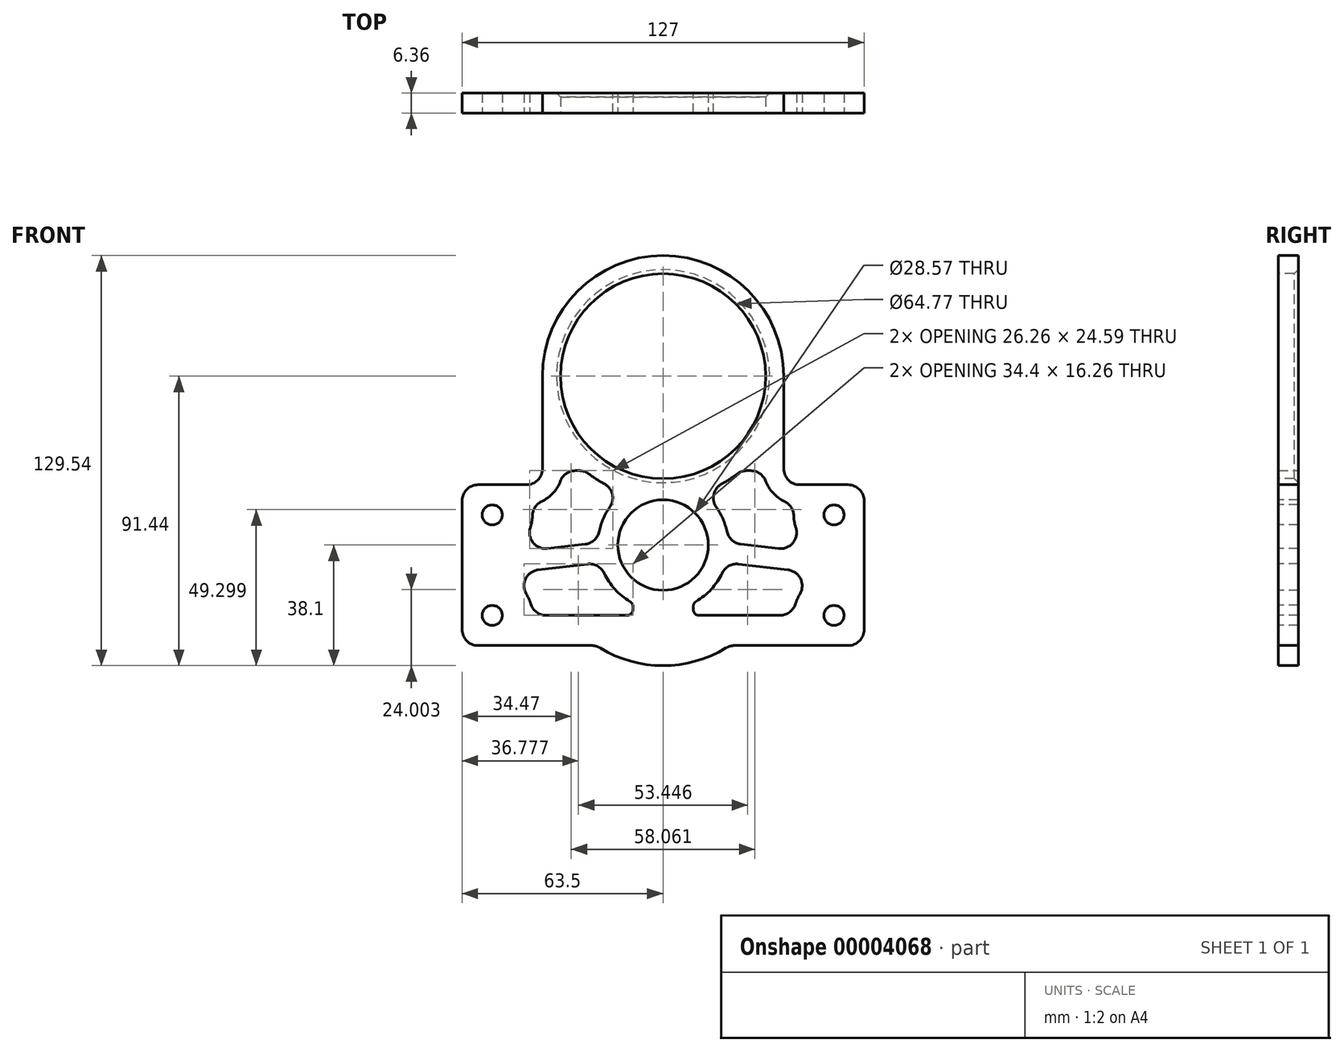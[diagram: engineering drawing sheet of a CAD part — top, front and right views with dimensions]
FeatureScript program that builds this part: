
annotation { "Feature Type Name" : "Feature", "Feature Type Description" : "" }
export const myFeature = defineFeature(function(context is Context, id is Id, definition is map)
    precondition{}
    {
        {
            var Q0;
            Q0=qCreatedBy(makeId("Front.planeOp"),FACE);
            var sketch = newSketch(context, id + "F0", { "sketchPlane" : qUnion([Q0])});
            skCircle(sketch, "E0", {"center": v(0, 0) * mm, "radius": 45.72 * mm, "construction": true});
            skCircle(sketch, "E1", {"center": v(0, 53.34) * mm, "radius": 7.62 * mm, "construction": true});
            skLineSegment(sketch, "E2", {"start": v(-38.1, 0) * mm, "end": v(-38.1, 53.34) * mm});
            skLineSegment(sketch, "E3", {"start": v(-38.1, 53.34) * mm, "end": v(0, 53.34) * mm, "construction": true});
            skLineSegment(sketch, "E4", {"start": v(0, 53.34) * mm, "end": v(38.1, 53.34) * mm, "construction": true});
            skLineSegment(sketch, "E5", {"start": v(38.1, 53.34) * mm, "end": v(38.1, 0) * mm});
            skArc(sketch, "E6", {"start": v(38.1, 53.34) * mm, "mid": v(0, 91.44) * mm, "end": v(-38.1, 53.34) * mm});
            skArc(sketch, "E7", {"start": v(-38.1, 0) * mm, "mid": v(0, -38.1) * mm, "end": v(38.1, 0) * mm});
            skCircle(sketch, "E8", {"center": v(0, 53.34) * mm, "radius": 25.4 * mm, "construction": true});
            skCircle(sketch, "E9", {"center": v(-25.4, 53.34) * mm, "radius": 2.54 * mm, "construction": true});
            skCircle(sketch, "E10", {"center": v(25.4, 53.34) * mm, "radius": 2.54 * mm, "construction": true});
            skSolve(sketch);
        }
        {
            var Q0;
            Q0=makeQuery(id+"F0.imprint","IMPRINT",FACE,{"disambiguationData":[TD([[makeQuery(id+"F0.imprint","IMPRINT",EDGE,{"derivedFrom":sQuery(id+"F0.wireOp",EDGE,"E2")}),-1.0]])]});
            extrude(context, id + "F1", {"entities" : qUnion([Q0]), "endBound" : BoundingType.SYMMETRIC, "depth" : 6.35 * mm});
        }
        {
            var Q0;
            Q0=makeQuery(id+"F1.opExtrude","CAP_FACE",FACE,{"disambiguationData":[OSD([sQuery(id+"F0.wireOp",EDGE,"E2"),sQuery(id+"F0.wireOp",EDGE,"E5"),sQuery(id+"F0.wireOp",EDGE,"E6"),sQuery(id+"F0.wireOp",EDGE,"E7")])],"isStart":false});
            var sketch = newSketch(context, id + "F2", { "sketchPlane" : qUnion([Q0])});
            skLineSegment(sketch, "E11.rect.bottom", {"start": v(63.5, -31.75) * mm, "end": v(-63.5, -31.75) * mm});
            skLineSegment(sketch, "E11.rect.top", {"start": v(63.5, 19.05) * mm, "end": v(-63.5, 19.05) * mm});
            skLineSegment(sketch, "E11.rect.left", {"start": v(63.5, -31.75) * mm, "end": v(63.5, 19.05) * mm});
            skLineSegment(sketch, "E11.rect.right", {"start": v(-63.5, -31.75) * mm, "end": v(-63.5, 19.05) * mm});
            skPoint(sketch, "E11.rect.middle", {"position": v(0, -6.35) * mm});
            skSolve(sketch);
        }
        {
            var Q0;
            {var subQ0=makeQuery(id+"F1.opExtrude","CAP_EDGE",EDGE,{"disambiguationData":[OSD([sQuery(id+"F0.wireOp",EDGE,"E7")])],"isStart":false});var subQ1=sQuery(id+"F2.wireOp",EDGE,"E11.rect.bottom");var subQ2=makeQuery(id+"F2.imprint","INTERSECT",VERTEX,{"disambiguationData":[OD(0.0)],"derivedFrom":[subQ0,subQ1]});var subQ9=sQuery(id+"F2.wireOp",EDGE,"E11.rect.left");var subQ16=sQuery(id+"F2.wireOp",EDGE,"E11.rect.right");Q0=qUnion([makeQuery(id+"F2.imprint","IMPRINT",FACE,{"disambiguationData":[TD([[makeQuery(id+"F2.imprint","IMPRINT",EDGE,{"derivedFrom":subQ9}),1.0]])]}),makeQuery(id+"F2.imprint","IMPRINT",FACE,{"disambiguationData":[TD([[makeQuery(id+"F2.imprint","IMPRINT",EDGE,{"derivedFrom":subQ16}),-1.0]])]}),makeQuery(id+"F2.imprint","IMPRINT",FACE,{"disambiguationData":[TD([[makeQuery(id+"F2.imprint","IMPRINT",EDGE,{"disambiguationData":[TD([[subQ2,-1.0]])],"derivedFrom":subQ1}),-1.0]])]})]);}
            var Q1;
            Q1=makeQuery(id+"F1.opExtrude","CAP_FACE",FACE,{"disambiguationData":[OSD([sQuery(id+"F0.wireOp",EDGE,"E2"),sQuery(id+"F0.wireOp",EDGE,"E5"),sQuery(id+"F0.wireOp",EDGE,"E6"),sQuery(id+"F0.wireOp",EDGE,"E7")])],"isStart":true});
            extrude(context, id + "F3", {"entities" : qUnion([Q0]), "operationType" : NewBodyOperationType.ADD, "endBound" : BoundingType.UP_TO_SURFACE, "oppositeDirection" : true, "endBoundEntityFace" : qUnion([Q1]), "depth" : 25.4 * mm});
        }
        {
            var Q0;
            Q0=makeQuery(id+"F3.boolean.opBoolean","INTERSECT",EDGE,{"derivedFrom":[makeQuery(id+"F1.opExtrude","SWEPT_FACE",FACE,{"disambiguationData":[OSD([sQuery(id+"F0.wireOp",EDGE,"E2")])]}),makeQuery(id+"F3.opExtrude","SWEPT_FACE",FACE,{"disambiguationData":[OSD([sQuery(id+"F2.wireOp",EDGE,"E11.rect.top")])]})]});
            var Q1;
            Q1=makeQuery(id+"F3.boolean.opBoolean","INTERSECT",EDGE,{"derivedFrom":[makeQuery(id+"F1.opExtrude","SWEPT_FACE",FACE,{"disambiguationData":[OSD([sQuery(id+"F0.wireOp",EDGE,"E5")])]}),makeQuery(id+"F3.opExtrude","SWEPT_FACE",FACE,{"disambiguationData":[OSD([sQuery(id+"F2.wireOp",EDGE,"E11.rect.top")])]})]});
            var Q2;
            Q2=makeQuery(id+"F3.boolean.opBoolean","INTERSECT",EDGE,{"disambiguationData":[OD(0.0)],"derivedFrom":[makeQuery(id+"F1.opExtrude","SWEPT_FACE",FACE,{"disambiguationData":[OSD([sQuery(id+"F0.wireOp",EDGE,"E7")])]}),makeQuery(id+"F3.opExtrude","SWEPT_FACE",FACE,{"disambiguationData":[OSD([sQuery(id+"F2.wireOp",EDGE,"E11.rect.bottom")])]})]});
            var Q3;
            Q3=makeQuery(id+"F3.boolean.opBoolean","INTERSECT",EDGE,{"disambiguationData":[OD(1.0)],"derivedFrom":[makeQuery(id+"F1.opExtrude","SWEPT_FACE",FACE,{"disambiguationData":[OSD([sQuery(id+"F0.wireOp",EDGE,"E7")])]}),makeQuery(id+"F3.opExtrude","SWEPT_FACE",FACE,{"disambiguationData":[OSD([sQuery(id+"F2.wireOp",EDGE,"E11.rect.bottom")])]})]});
            var Q4;
            Q4=makeQuery(id+"F3.opExtrude","SWEPT_EDGE",EDGE,{"disambiguationData":[OSD([sQuery(id+"F2.wireOp",EDGE,"E11.rect.top"),sQuery(id+"F2.wireOp",EDGE,"E11.rect.right")])]});
            var Q5;
            Q5=makeQuery(id+"F3.opExtrude","SWEPT_EDGE",EDGE,{"disambiguationData":[OSD([sQuery(id+"F2.wireOp",EDGE,"E11.rect.top"),sQuery(id+"F2.wireOp",EDGE,"E11.rect.left")])]});
            var Q6;
            Q6=makeQuery(id+"F3.opExtrude","SWEPT_EDGE",EDGE,{"disambiguationData":[OSD([sQuery(id+"F2.wireOp",EDGE,"E11.rect.bottom"),sQuery(id+"F2.wireOp",EDGE,"E11.rect.left")])]});
            var Q7;
            Q7=makeQuery(id+"F3.opExtrude","SWEPT_EDGE",EDGE,{"disambiguationData":[OSD([sQuery(id+"F2.wireOp",EDGE,"E11.rect.bottom"),sQuery(id+"F2.wireOp",EDGE,"E11.rect.right")])]});
            fillet(context, id + "F4", {"entities" : qUnion([Q0, Q1, Q2, Q3, Q4, Q5, Q6, Q7]), "radius" : 5.08 * mm, "tangentPropagation" : true, "allowEdgeOverflow" : false});
        }
        {
            var Q0;
            Q0=makeQuery(id+"F3.boolean.opBoolean","MERGE",FACE,{"derivedFrom":[makeQuery(id+"F1.opExtrude","CAP_FACE",FACE,{"disambiguationData":[OSD([sQuery(id+"F0.wireOp",EDGE,"E2"),sQuery(id+"F0.wireOp",EDGE,"E5"),sQuery(id+"F0.wireOp",EDGE,"E6"),sQuery(id+"F0.wireOp",EDGE,"E7")])],"isStart":false}),makeQuery(id+"F3.opExtrude","CAP_FACE",FACE,{"disambiguationData":[OSD([sQuery(id+"F2.wireOp",EDGE,"E11.rect.bottom"),sQuery(id+"F2.wireOp",EDGE,"E11.rect.top"),sQuery(id+"F2.wireOp",EDGE,"E11.rect.left"),sQuery(id+"F2.wireOp",EDGE,"E11.rect.right")])],"isStart":true})]});
            var sketch = newSketch(context, id + "F5", { "sketchPlane" : qUnion([Q0])});
            skCircle(sketch, "E12", {"center": v(0, 0) * mm, "radius": 14.29 * mm});
            skCircle(sketch, "E13", {"center": v(0, 53.34) * mm, "radius": 32.39 * mm});
            skCircle(sketch, "E14", {"center": v(0, 53.34) * mm, "radius": 25.4 * mm, "construction": true});
            skLineSegment(sketch, "E15", {"start": v(-38.1, 53.34) * mm, "end": v(38.1, 53.34) * mm, "construction": true});
            skCircle(sketch, "E16", {"center": v(-25.4, 53.34) * mm, "radius": 2.54 * mm, "construction": true});
            skCircle(sketch, "E17", {"center": v(25.4, 53.34) * mm, "radius": 2.54 * mm, "construction": true});
            skCircle(sketch, "E18", {"center": v(-53.98, 9.52) * mm, "radius": 3.18 * mm});
            skCircle(sketch, "E19", {"center": v(-53.97, -22.23) * mm, "radius": 3.18 * mm});
            skCircle(sketch, "E20", {"center": v(53.98, 9.52) * mm, "radius": 3.18 * mm});
            skCircle(sketch, "E21", {"center": v(53.98, -22.22) * mm, "radius": 3.18 * mm});
            skLineSegment(sketch, "E22", {"start": v(-53.98, 9.52) * mm, "end": v(0, 9.52) * mm, "construction": true});
            skLineSegment(sketch, "E23", {"start": v(0, 9.52) * mm, "end": v(53.98, 9.52) * mm, "construction": true});
            skSolve(sketch);
        }
        {
            var Q0;
            {Q0=qUnion([makeQuery(id+"F5.imprint","IMPRINT",FACE,{"disambiguationData":[TD([[makeQuery(id+"F5.imprint","IMPRINT",EDGE,{"derivedFrom":sQuery(id+"F5.wireOp",EDGE,"E12")}),1.0]])]}),makeQuery(id+"F5.imprint","IMPRINT",FACE,{"disambiguationData":[TD([[makeQuery(id+"F5.imprint","IMPRINT",EDGE,{"derivedFrom":sQuery(id+"F5.wireOp",EDGE,"E13")}),1.0]])]}),makeQuery(id+"F5.imprint","IMPRINT",FACE,{"disambiguationData":[TD([[makeQuery(id+"F5.imprint","IMPRINT",EDGE,{"derivedFrom":sQuery(id+"F5.wireOp",EDGE,"E18")}),1.0]])]}),makeQuery(id+"F5.imprint","IMPRINT",FACE,{"disambiguationData":[TD([[makeQuery(id+"F5.imprint","IMPRINT",EDGE,{"derivedFrom":sQuery(id+"F5.wireOp",EDGE,"E19")}),1.0]])]}),makeQuery(id+"F5.imprint","IMPRINT",FACE,{"disambiguationData":[TD([[makeQuery(id+"F5.imprint","IMPRINT",EDGE,{"derivedFrom":sQuery(id+"F5.wireOp",EDGE,"E20")}),1.0]])]}),makeQuery(id+"F5.imprint","IMPRINT",FACE,{"disambiguationData":[TD([[makeQuery(id+"F5.imprint","IMPRINT",EDGE,{"derivedFrom":sQuery(id+"F5.wireOp",EDGE,"E21")}),1.0]])]})]);}
            extrude(context, id + "F6", {"entities" : qUnion([Q0]), "operationType" : NewBodyOperationType.REMOVE, "endBound" : BoundingType.THROUGH_ALL, "oppositeDirection" : true, "depth" : 25.4 * mm});
        }
        {
            var Q0;
            Q0=makeQuery(id+"F3.boolean.opBoolean","MERGE",FACE,{"derivedFrom":[makeQuery(id+"F1.opExtrude","CAP_FACE",FACE,{"disambiguationData":[OSD([sQuery(id+"F0.wireOp",EDGE,"E2"),sQuery(id+"F0.wireOp",EDGE,"E5"),sQuery(id+"F0.wireOp",EDGE,"E6"),sQuery(id+"F0.wireOp",EDGE,"E7")])],"isStart":false}),makeQuery(id+"F3.opExtrude","CAP_FACE",FACE,{"disambiguationData":[OSD([sQuery(id+"F2.wireOp",EDGE,"E11.rect.bottom"),sQuery(id+"F2.wireOp",EDGE,"E11.rect.top"),sQuery(id+"F2.wireOp",EDGE,"E11.rect.left"),sQuery(id+"F2.wireOp",EDGE,"E11.rect.right")])],"isStart":true})]});
            var sketch = newSketch(context, id + "F7", { "sketchPlane" : qUnion([Q0])});
            skCircle(sketch, "E24", {"center": v(-53.98, 9.52) * mm, "radius": 6.35 * mm});
            skCircle(sketch, "E25", {"center": v(53.98, 9.52) * mm, "radius": 6.35 * mm});
            skCircle(sketch, "E26", {"center": v(53.98, -22.22) * mm, "radius": 6.35 * mm});
            skCircle(sketch, "E27", {"center": v(-53.97, -22.23) * mm, "radius": 6.35 * mm});
            skSolve(sketch);
        }
        {
            var Q0;
            Q0=makeQuery(id+"F3.boolean.opBoolean","MERGE",FACE,{"derivedFrom":[makeQuery(id+"F1.opExtrude","CAP_FACE",FACE,{"disambiguationData":[OSD([sQuery(id+"F0.wireOp",EDGE,"E2"),sQuery(id+"F0.wireOp",EDGE,"E5"),sQuery(id+"F0.wireOp",EDGE,"E6"),sQuery(id+"F0.wireOp",EDGE,"E7")])],"isStart":false}),makeQuery(id+"F3.opExtrude","CAP_FACE",FACE,{"disambiguationData":[OSD([sQuery(id+"F2.wireOp",EDGE,"E11.rect.bottom"),sQuery(id+"F2.wireOp",EDGE,"E11.rect.top"),sQuery(id+"F2.wireOp",EDGE,"E11.rect.left"),sQuery(id+"F2.wireOp",EDGE,"E11.rect.right")])],"isStart":true})]});
            var sketch = newSketch(context, id + "F8", { "sketchPlane" : qUnion([Q0])});
            skCircle(sketch, "E28.0", {"center": v(0, 0) * mm, "radius": 20.64 * mm});
            skCircle(sketch, "E29.0", {"center": v(0, 53.34) * mm, "radius": 38.74 * mm});
            skCircle(sketch, "E30.0", {"center": v(-25.4, 53.34) * mm, "radius": 8.9 * mm});
            skCircle(sketch, "E31.0", {"center": v(-53.98, 9.52) * mm, "radius": 12.7 * mm});
            skCircle(sketch, "E32.0", {"center": v(-53.97, -22.23) * mm, "radius": 12.7 * mm});
            skCircle(sketch, "E33", {"center": v(0, 0) * mm, "radius": 31.75 * mm});
            skCircle(sketch, "E34", {"center": v(0, 53.34) * mm, "radius": 31.75 * mm});
            skLineSegment(sketch, "E35", {"start": v(-53.97, -22.23) * mm, "end": v(0, -22.23) * mm});
            skLineSegment(sketch, "E36", {"start": v(-53.98, 9.52) * mm, "end": v(-53.98, -22.23) * mm});
            skLineSegment(sketch, "E37", {"start": v(-53.98, 9.52) * mm, "end": v(0, 9.53) * mm});
            skArc(sketch, "E38.0", {"start": v(-31.75, 24.13) * mm, "mid": v(-40.57, 13) * mm, "end": v(-53.42, 19.05) * mm});
            skLineSegment(sketch, "E38.1", {"start": v(-31.75, 24.13) * mm, "end": v(-31.75, 53.34) * mm});
            skLineSegment(sketch, "E39", {"start": v(0, 85.1) * mm, "end": v(0, -38.1) * mm});
            skLineSegment(sketch, "E40", {"start": v(-3.18, 84.93) * mm, "end": v(-3.17, -31.6) * mm});
            skLineSegment(sketch, "E41", {"start": v(-17.23, 26.67) * mm, "end": v(0, 26.67) * mm});
            skLineSegment(sketch, "E42", {"start": v(-17.23, 26.67) * mm, "end": v(-32.04, 26.67) * mm});
            skLineSegment(sketch, "E43", {"start": v(-33.28, 29.84) * mm, "end": v(0, 29.84) * mm});
            skLineSegment(sketch, "E44", {"start": v(-31.77, 23.5) * mm, "end": v(0, 23.5) * mm});
            skLineSegment(sketch, "E45", {"start": v(-53.98, -6.35) * mm, "end": v(0, 0) * mm});
            skLineSegment(sketch, "E46.0", {"start": v(-53.98, -3.15) * mm, "end": v(0, 3.2) * mm});
            skLineSegment(sketch, "E47.0", {"start": v(-53.98, -9.55) * mm, "end": v(0, -3.2) * mm});
            skLineSegment(sketch, "E48", {"start": v(-9.53, -18.3) * mm, "end": v(-9.53, -22.23) * mm});
            skSolve(sketch);
        }
        {
            var Q0;
            {var subQ3=sQuery(id+"F8.wireOp",EDGE,"E28.0");var subQ5=sQuery(id+"F8.wireOp",EDGE,"E37");var subQ7=makeQuery(id+"F8.imprint","INTERSECT",VERTEX,{"derivedFrom":[subQ3,subQ5]});Q0=makeQuery(id+"F8.imprint","IMPRINT",FACE,{"disambiguationData":[TD([[makeQuery(id+"F8.imprint","IMPRINT",EDGE,{"disambiguationData":[TD([[subQ7,-1.0]])],"derivedFrom":subQ3}),-1.0]])]});}
            var Q1;
            {var subQ3=sQuery(id+"F8.wireOp",EDGE,"E31.0");var subQ5=sQuery(id+"F8.wireOp",EDGE,"E37");var subQ7=makeQuery(id+"F8.imprint","INTERSECT",VERTEX,{"derivedFrom":[subQ3,subQ5]});Q1=makeQuery(id+"F8.imprint","IMPRINT",FACE,{"disambiguationData":[TD([[makeQuery(id+"F8.imprint","IMPRINT",EDGE,{"disambiguationData":[TD([[subQ7,1.0]])],"derivedFrom":subQ3}),-1.0]])]});}
            var Q2;
            {var subQ0=sQuery(id+"F8.wireOp",EDGE,"E47.0");var subQ3=sQuery(id+"F8.wireOp",EDGE,"E32.0");var subQ4=makeQuery(id+"F8.imprint","INTERSECT",VERTEX,{"derivedFrom":[subQ3,subQ0]});Q2=makeQuery(id+"F8.imprint","IMPRINT",FACE,{"disambiguationData":[TD([[makeQuery(id+"F8.imprint","IMPRINT",EDGE,{"disambiguationData":[TD([[subQ4,1.0]])],"derivedFrom":subQ3}),-1.0]])]});}
            var Q3;
            {var subQ0=sQuery(id+"F8.wireOp",EDGE,"E47.0");var subQ3=sQuery(id+"F8.wireOp",EDGE,"E28.0");var subQ4=makeQuery(id+"F8.imprint","INTERSECT",VERTEX,{"derivedFrom":[subQ3,subQ0]});Q3=makeQuery(id+"F8.imprint","IMPRINT",FACE,{"disambiguationData":[TD([[makeQuery(id+"F8.imprint","IMPRINT",EDGE,{"disambiguationData":[TD([[subQ4,-1.0]])],"derivedFrom":subQ3}),-1.0]])]});}
            var Q4;
            {var subQ3=sQuery(id+"F8.wireOp",EDGE,"E28.0");var subQ5=sQuery(id+"F8.wireOp",EDGE,"E37");var subQ7=makeQuery(id+"F8.imprint","INTERSECT",VERTEX,{"derivedFrom":[subQ3,subQ5]});Q4=makeQuery(id+"F8.imprint","IMPRINT",FACE,{"disambiguationData":[TD([[makeQuery(id+"F8.imprint","IMPRINT",EDGE,{"disambiguationData":[TD([[subQ7,-1.0]])],"derivedFrom":subQ3}),-1.0]])]});}
            var Q5;
            {var subQ5=sQuery(id+"F8.wireOp",EDGE,"E38.0");var subQ7=sQuery(id+"F8.wireOp",EDGE,"E31.0");var subQ8=makeQuery(id+"F8.imprint","INTERSECT",VERTEX,{"derivedFrom":[subQ7,subQ5]});Q5=makeQuery(id+"F8.imprint","IMPRINT",FACE,{"disambiguationData":[TD([[makeQuery(id+"F8.imprint","IMPRINT",EDGE,{"disambiguationData":[TD([[subQ8,1.0]])],"derivedFrom":subQ7}),-1.0]])]});}
            var Q6;
            {var subQ3=sQuery(id+"F8.wireOp",EDGE,"E28.0");var subQ5=sQuery(id+"F8.wireOp",EDGE,"E29.0");var subQ7=makeQuery(id+"F8.imprint","INTERSECT",VERTEX,{"disambiguationData":[OD(1.0)],"derivedFrom":[subQ3,subQ5]});Q6=makeQuery(id+"F8.imprint","IMPRINT",FACE,{"disambiguationData":[TD([[makeQuery(id+"F8.imprint","IMPRINT",EDGE,{"disambiguationData":[TD([[subQ7,-1.0]])],"derivedFrom":subQ3}),-1.0]])]});}
            extrude(context, id + "F9", {"entities" : qUnion([Q0, Q1, Q2, Q3, Q4, Q5, Q6]), "operationType" : NewBodyOperationType.REMOVE, "endBound" : BoundingType.THROUGH_ALL, "oppositeDirection" : true, "depth" : 25.4 * mm});
        }
        {
            var Q0;
            Q0=makeQuery(id+"F9.boolean.opBoolean","COPY",EDGE,{"derivedFrom":makeQuery(id+"F9.opExtrude","SWEPT_EDGE",EDGE,{"disambiguationData":[OSD([sQuery(id+"F8.wireOp",EDGE,"E32.0"),sQuery(id+"F8.wireOp",EDGE,"E35")])]})});
            var Q1;
            Q1=makeQuery(id+"F9.boolean.opBoolean","COPY",EDGE,{"derivedFrom":makeQuery(id+"F9.opExtrude","SWEPT_EDGE",EDGE,{"disambiguationData":[OSD([sQuery(id+"F8.wireOp",EDGE,"E34"),sQuery(id+"F8.wireOp",EDGE,"E40")])]})});
            var Q2;
            {var subQ0=sQuery(id+"F8.wireOp",EDGE,"E29.0");Q2=qUnion([makeQuery(id+"F9.boolean.opBoolean","COPY",EDGE,{"derivedFrom":makeQuery(id+"F9.opExtrude","SWEPT_EDGE",EDGE,{"disambiguationData":[OSD([subQ0,sQuery(id+"F8.wireOp",EDGE,"E44")])]})}),makeQuery(id+"F9.boolean.opBoolean","COPY",EDGE,{"derivedFrom":makeQuery(id+"F9.opExtrude","SWEPT_EDGE",EDGE,{"disambiguationData":[OSD([sQuery(id+"F8.wireOp",EDGE,"E28.0"),subQ0])]})})]);}
            var Q3;
            Q3=makeQuery(id+"F9.boolean.opBoolean","COPY",EDGE,{"derivedFrom":makeQuery(id+"F9.opExtrude","SWEPT_EDGE",EDGE,{"disambiguationData":[OSD([sQuery(id+"F8.wireOp",EDGE,"E28.0"),sQuery(id+"F8.wireOp",EDGE,"E47.0")])]})});
            var Q4;
            Q4=makeQuery(id+"F9.boolean.opBoolean","COPY",EDGE,{"derivedFrom":makeQuery(id+"F9.opExtrude","SWEPT_EDGE",EDGE,{"disambiguationData":[OSD([sQuery(id+"F8.wireOp",EDGE,"E28.0"),sQuery(id+"F8.wireOp",EDGE,"E46.0")])]})});
            var Q5;
            Q5=makeQuery(id+"F9.boolean.opBoolean","COPY",EDGE,{"derivedFrom":makeQuery(id+"F9.opExtrude","SWEPT_EDGE",EDGE,{"disambiguationData":[OSD([sQuery(id+"F8.wireOp",EDGE,"E31.0"),sQuery(id+"F8.wireOp",EDGE,"E38.0")])]})});
            var Q6;
            {var subQ0=sQuery(id+"F8.wireOp",EDGE,"E29.0");Q6=qUnion([makeQuery(id+"F9.boolean.opBoolean","COPY",EDGE,{"derivedFrom":makeQuery(id+"F9.opExtrude","SWEPT_EDGE",EDGE,{"disambiguationData":[OSD([subQ0,sQuery(id+"F8.wireOp",EDGE,"E44")])]})}),makeQuery(id+"F9.boolean.opBoolean","COPY",EDGE,{"derivedFrom":makeQuery(id+"F9.opExtrude","SWEPT_EDGE",EDGE,{"disambiguationData":[OSD([sQuery(id+"F8.wireOp",EDGE,"E28.0"),subQ0])]})})]);}
            var Q7;
            Q7=makeQuery(id+"F9.boolean.opBoolean","COPY",EDGE,{"derivedFrom":makeQuery(id+"F9.opExtrude","SWEPT_EDGE",EDGE,{"disambiguationData":[OSD([sQuery(id+"F8.wireOp",EDGE,"E30.0"),sQuery(id+"F8.wireOp",EDGE,"E38.1")])]})});
            var Q8;
            Q8=makeQuery(id+"F9.boolean.opBoolean","COPY",EDGE,{"derivedFrom":makeQuery(id+"F9.opExtrude","SWEPT_EDGE",EDGE,{"disambiguationData":[OSD([sQuery(id+"F8.wireOp",EDGE,"E38.0"),sQuery(id+"F8.wireOp",EDGE,"E44")])]})});
            var Q9;
            Q9=makeQuery(id+"F9.boolean.opBoolean","COPY",EDGE,{"derivedFrom":makeQuery(id+"F9.opExtrude","SWEPT_EDGE",EDGE,{"disambiguationData":[OSD([sQuery(id+"F8.wireOp",EDGE,"E38.1"),sQuery(id+"F8.wireOp",EDGE,"E43")])]})});
            var Q10;
            Q10=makeQuery(id+"F9.boolean.opBoolean","COPY",EDGE,{"derivedFrom":makeQuery(id+"F9.opExtrude","SWEPT_EDGE",EDGE,{"disambiguationData":[OSD([sQuery(id+"F8.wireOp",EDGE,"E31.0"),sQuery(id+"F8.wireOp",EDGE,"E38.0")])]})});
            var Q11;
            {var subQ0=sQuery(id+"F8.wireOp",EDGE,"E29.0");Q11=qUnion([makeQuery(id+"F9.boolean.opBoolean","COPY",EDGE,{"derivedFrom":makeQuery(id+"F9.opExtrude","SWEPT_EDGE",EDGE,{"disambiguationData":[OSD([subQ0,sQuery(id+"F8.wireOp",EDGE,"E44")])]})}),makeQuery(id+"F9.boolean.opBoolean","COPY",EDGE,{"derivedFrom":makeQuery(id+"F9.opExtrude","SWEPT_EDGE",EDGE,{"disambiguationData":[OSD([sQuery(id+"F8.wireOp",EDGE,"E28.0"),subQ0])]})})]);}
            var Q12;
            Q12=makeQuery(id+"F9.boolean.opBoolean","COPY",EDGE,{"derivedFrom":makeQuery(id+"F9.opExtrude","SWEPT_EDGE",EDGE,{"disambiguationData":[OSD([sQuery(id+"F8.wireOp",EDGE,"E30.0"),sQuery(id+"F8.wireOp",EDGE,"E34")])]})});
            var Q13;
            Q13=makeQuery(id+"F9.boolean.opBoolean","COPY",EDGE,{"derivedFrom":makeQuery(id+"F9.opExtrude","SWEPT_EDGE",EDGE,{"disambiguationData":[OSD([sQuery(id+"F8.wireOp",EDGE,"E34"),sQuery(id+"F8.wireOp",EDGE,"E40")])]})});
            var Q14;
            {var subQ0=sQuery(id+"F8.wireOp",EDGE,"E29.0");Q14=qUnion([makeQuery(id+"F9.boolean.opBoolean","COPY",EDGE,{"derivedFrom":makeQuery(id+"F9.opExtrude","SWEPT_EDGE",EDGE,{"disambiguationData":[OSD([subQ0,sQuery(id+"F8.wireOp",EDGE,"E44")])]})}),makeQuery(id+"F9.boolean.opBoolean","COPY",EDGE,{"derivedFrom":makeQuery(id+"F9.opExtrude","SWEPT_EDGE",EDGE,{"disambiguationData":[OSD([sQuery(id+"F8.wireOp",EDGE,"E28.0"),subQ0])]})})]);}
            var Q15;
            Q15=makeQuery(id+"F9.boolean.opBoolean","COPY",EDGE,{"derivedFrom":makeQuery(id+"F9.opExtrude","SWEPT_EDGE",EDGE,{"disambiguationData":[OSD([sQuery(id+"F8.wireOp",EDGE,"E31.0"),sQuery(id+"F8.wireOp",EDGE,"E46.0")])]})});
            var Q16;
            Q16=makeQuery(id+"F9.boolean.opBoolean","COPY",EDGE,{"derivedFrom":makeQuery(id+"F9.opExtrude","SWEPT_EDGE",EDGE,{"disambiguationData":[OSD([sQuery(id+"F8.wireOp",EDGE,"E32.0"),sQuery(id+"F8.wireOp",EDGE,"E47.0")])]})});
            var Q17;
            Q17=makeQuery(id+"F9.boolean.opBoolean","COPY",EDGE,{"derivedFrom":makeQuery(id+"F9.opExtrude","SWEPT_EDGE",EDGE,{"disambiguationData":[OSD([sQuery(id+"F8.wireOp",EDGE,"E32.0"),sQuery(id+"F8.wireOp",EDGE,"E35")])]})});
            fillet(context, id + "F10", {"entities" : qUnion([Q0, Q1, Q2, Q3, Q4, Q5, Q6, Q7, Q8, Q9, Q10, Q11, Q12, Q13, Q14, Q15, Q16, Q17]), "radius" : 5.08 * mm, "tangentPropagation" : true, "allowEdgeOverflow" : false});
        }
        {
            var Q0;
            Q0=makeQuery(id+"F9.boolean.opBoolean","COPY",EDGE,{"derivedFrom":makeQuery(id+"F9.opExtrude","SWEPT_EDGE",EDGE,{"disambiguationData":[OSD([sQuery(id+"F8.wireOp",EDGE,"E28.0"),sQuery(id+"F8.wireOp",EDGE,"E48")])]})});
            var Q1;
            Q1=makeQuery(id+"F9.boolean.opBoolean","COPY",EDGE,{"derivedFrom":makeQuery(id+"F9.opExtrude","SWEPT_EDGE",EDGE,{"disambiguationData":[OSD([sQuery(id+"F8.wireOp",EDGE,"E35"),sQuery(id+"F8.wireOp",EDGE,"E48")])]})});
            var Q2;
            Q2=makeQuery(id+"F9.boolean.opBoolean","COPY",EDGE,{"derivedFrom":makeQuery(id+"F9.opExtrude","SWEPT_EDGE",EDGE,{"disambiguationData":[OSD([sQuery(id+"F8.wireOp",EDGE,"E28.0"),sQuery(id+"F8.wireOp",EDGE,"E48")])]})});
            var Q3;
            Q3=makeQuery(id+"F9.boolean.opBoolean","COPY",EDGE,{"derivedFrom":makeQuery(id+"F9.opExtrude","SWEPT_EDGE",EDGE,{"disambiguationData":[OSD([sQuery(id+"F8.wireOp",EDGE,"E40"),sQuery(id+"F8.wireOp",EDGE,"E44")])]})});
            var Q4;
            {var subQ0=sQuery(id+"F8.wireOp",EDGE,"E29.0");var subQ1=sQuery(id+"F8.wireOp",EDGE,"E40");Q4=makeQuery(id+"F9.boolean.opBoolean","COPY",EDGE,{"derivedFrom":makeQuery(id+"F9.opExtrude","SWEPT_EDGE",EDGE,{"disambiguationData":[OSD([subQ0,subQ1]),TDD([makeQuery(id+"F8.imprint","INTERSECT",VERTEX,{"disambiguationData":[OD(1.0)],"derivedFrom":[subQ0,subQ1]})])]})});}
            var Q5;
            Q5=makeQuery(id+"F9.boolean.opBoolean","COPY",EDGE,{"derivedFrom":makeQuery(id+"F9.opExtrude","SWEPT_EDGE",EDGE,{"disambiguationData":[OSD([sQuery(id+"F8.wireOp",EDGE,"E40"),sQuery(id+"F8.wireOp",EDGE,"E43")])]})});
            fillet(context, id + "F11", {"entities" : qUnion([Q0, Q1, Q2, Q3, Q4, Q5]), "radius" : 1.9 * mm, "tangentPropagation" : true, "allowEdgeOverflow" : false});
        }
        {
            var Q0;
            Q0=qCreatedBy(makeId("Right.planeOp"),FACE);
            var sketch = newSketch(context, id + "F12", { "sketchPlane" : qUnion([Q0])});
            skLineSegment(sketch, "E49.rect.bottom", {"start": v(12.7, -52.07) * mm, "end": v(-12.7, -52.07) * mm});
            skLineSegment(sketch, "E49.rect.top", {"start": v(12.7, 100.33) * mm, "end": v(-12.7, 100.33) * mm});
            skLineSegment(sketch, "E49.rect.left", {"start": v(12.7, -52.07) * mm, "end": v(12.7, 100.33) * mm});
            skLineSegment(sketch, "E49.rect.right", {"start": v(-12.7, -52.07) * mm, "end": v(-12.7, 100.33) * mm});
            skPoint(sketch, "E49.rect.middle", {"position": v(0, 24.13) * mm});
            skSolve(sketch);
        }
        {
            var Q0;
            Q0=makeQuery(id+"F12.imprint","IMPRINT",FACE,{"disambiguationData":[TD([[makeQuery(id+"F12.imprint","IMPRINT",EDGE,{"derivedFrom":sQuery(id+"F12.wireOp",EDGE,"E49.rect.bottom")}),-1.0]])]});
            extrude(context, id + "F13", {"entities" : qUnion([Q0]), "operationType" : NewBodyOperationType.REMOVE, "endBound" : BoundingType.THROUGH_ALL, "depth" : 25.4 * mm});
        }
        {
            var Q0;
            Q0=makeQuery(id+"F1.opExtrude","SWEPT_BODY",BODY,{"disambiguationData":[OSD([sQuery(id+"F0.wireOp",EDGE,"E2"),sQuery(id+"F0.wireOp",EDGE,"E5"),sQuery(id+"F0.wireOp",EDGE,"E6"),sQuery(id+"F0.wireOp",EDGE,"E7")])]});
            var Q1;
            Q1=qCreatedBy(makeId("Right.planeOp"),FACE);
            mirror(context, id + "F14", {"entities" : qUnion([Q0]), "mirrorPlane" : qUnion([Q1])});
        }
        {
            var Q0;
            Q0=makeQuery(id+"F1.opExtrude","SWEPT_BODY",BODY,{"disambiguationData":[OSD([sQuery(id+"F0.wireOp",EDGE,"E2"),sQuery(id+"F0.wireOp",EDGE,"E5"),sQuery(id+"F0.wireOp",EDGE,"E6"),sQuery(id+"F0.wireOp",EDGE,"E7")])]});
            var Q1;
            Q1=makeQuery(id+"F14.opPattern","COPY",BODY,{"derivedFrom":makeQuery(id+"F1.opExtrude","SWEPT_BODY",BODY,{"disambiguationData":[OSD([sQuery(id+"F0.wireOp",EDGE,"E2"),sQuery(id+"F0.wireOp",EDGE,"E5"),sQuery(id+"F0.wireOp",EDGE,"E6"),sQuery(id+"F0.wireOp",EDGE,"E7")])]}),"instanceName":"1"});
            booleanBodies(context, id + "F15", {"operationType" : BooleanOperationType.UNION, "tools" : qUnion([Q0, Q1])});
        }
        {
            var Q0;
            {var subQ0=makeQuery(id+"F6.boolean.opBoolean","COPY",EDGE,{"derivedFrom":makeQuery(id+"F6.opExtrude","CAP_EDGE",EDGE,{"disambiguationData":[OSD([sQuery(id+"F5.wireOp",EDGE,"E13")])],"isStart":true})});Q0=makeQuery(id+"F15.opBoolean","MERGE",EDGE,{"derivedFrom":[subQ0,makeQuery(id+"F14.opPattern","COPY",EDGE,{"derivedFrom":subQ0,"instanceName":"1"})]});}
            var Q1;
            {var subQ0=makeQuery(id+"F6.boolean.opBoolean","INTERSECT",EDGE,{"derivedFrom":[makeQuery(id+"F3.boolean.opBoolean","MERGE",FACE,{"derivedFrom":[makeQuery(id+"F1.opExtrude","CAP_FACE",FACE,{"disambiguationData":[OSD([sQuery(id+"F0.wireOp",EDGE,"E2"),sQuery(id+"F0.wireOp",EDGE,"E5"),sQuery(id+"F0.wireOp",EDGE,"E6"),sQuery(id+"F0.wireOp",EDGE,"E7")])],"isStart":true}),makeQuery(id+"F3.opExtrude","CAP_FACE",FACE,{"disambiguationData":[OSD([sQuery(id+"F2.wireOp",EDGE,"E11.rect.bottom"),sQuery(id+"F2.wireOp",EDGE,"E11.rect.top"),sQuery(id+"F2.wireOp",EDGE,"E11.rect.left"),sQuery(id+"F2.wireOp",EDGE,"E11.rect.right")])],"isStart":false})]}),makeQuery(id+"F6.opExtrude","SWEPT_FACE",FACE,{"disambiguationData":[OSD([sQuery(id+"F5.wireOp",EDGE,"E13")])]})]});Q1=makeQuery(id+"F15.opBoolean","MERGE",EDGE,{"derivedFrom":[subQ0,makeQuery(id+"F14.opPattern","COPY",EDGE,{"derivedFrom":subQ0,"instanceName":"1"})]});}
            chamfer(context, id + "F16", {"entities" : qUnion([Q0, Q1]), "width" : 1.27 * mm, "tangentPropagation" : true});
        }
    });
